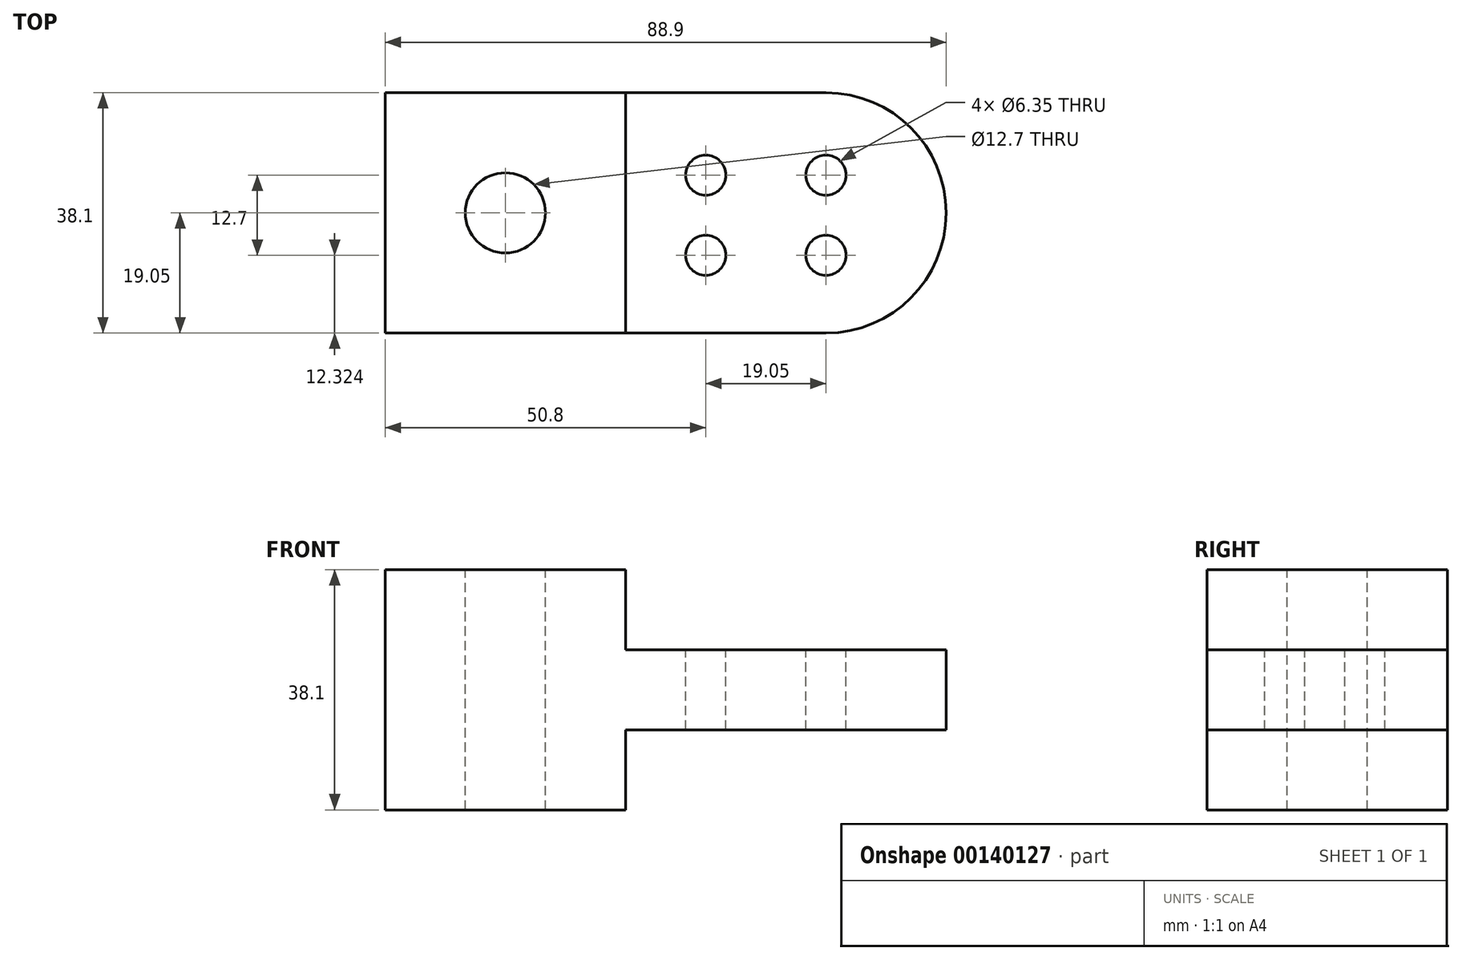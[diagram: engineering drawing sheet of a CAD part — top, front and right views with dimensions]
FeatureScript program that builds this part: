
annotation { "Feature Type Name" : "Feature", "Feature Type Description" : "" }
export const myFeature = defineFeature(function(context is Context, id is Id, definition is map)
    precondition{}
    {
        {
            var Q0;
            Q0=qCreatedBy(makeId("Top.planeOp"),FACE);
            var sketch = newSketch(context, id + "F0", { "sketchPlane" : qUnion([Q0])});
            skLineSegment(sketch, "E0.bottom", {"start": v(0, 0) * mm, "end": v(38.1, 0) * mm});
            skLineSegment(sketch, "E0.top", {"start": v(0, 38.1) * mm, "end": v(38.1, 38.1) * mm});
            skLineSegment(sketch, "E0.left", {"start": v(0, 0) * mm, "end": v(0, 38.1) * mm});
            skLineSegment(sketch, "E0.right", {"start": v(38.1, 0) * mm, "end": v(38.1, 38.1) * mm});
            skLineSegment(sketch, "E1.bottom", {"start": v(38.1, 38.1) * mm, "end": v(69.85, 38.1) * mm});
            skLineSegment(sketch, "E1.top", {"start": v(38.1, 0) * mm, "end": v(69.85, 0) * mm});
            skLineSegment(sketch, "E1.left", {"start": v(38.1, 38.1) * mm, "end": v(38.1, 0) * mm});
            skLineSegment(sketch, "E1.right", {"start": v(69.85, 38.1) * mm, "end": v(69.85, 0) * mm});
            skArc(sketch, "E2", {"start": v(69.85, 0) * mm, "mid": v(88.9, 19.05) * mm, "end": v(69.85, 38.1) * mm});
            skSolve(sketch);
        }
        {
            var Q0;
            Q0=makeQuery(id+"F0.imprint","IMPRINT",FACE,{"disambiguationData":[TD([[makeQuery(id+"F0.imprint","IMPRINT",EDGE,{"derivedFrom":sQuery(id+"F0.wireOp",EDGE,"E0.bottom")}),1.0]])]});
            extrude(context, id + "F1", {"entities" : qUnion([Q0]), "endBound" : BoundingType.SYMMETRIC, "depth" : 38.1 * mm});
        }
        {
            var Q0;
            Q0=makeQuery(id+"F0.imprint","IMPRINT",FACE,{"disambiguationData":[TD([[makeQuery(id+"F0.imprint","IMPRINT",EDGE,{"derivedFrom":sQuery(id+"F0.wireOp",EDGE,"E1.bottom")}),-1.0]])]});
            var Q1;
            Q1=makeQuery(id+"F0.imprint","IMPRINT",FACE,{"disambiguationData":[TD([[makeQuery(id+"F0.imprint","IMPRINT",EDGE,{"derivedFrom":sQuery(id+"F0.wireOp",EDGE,"E1.right")}),1.0]])]});
            extrude(context, id + "F2", {"entities" : qUnion([Q0, Q1]), "operationType" : NewBodyOperationType.ADD, "endBound" : BoundingType.SYMMETRIC, "depth" : 12.7 * mm});
        }
        {
            var Q0;
            Q0=makeQuery(id+"F1.opExtrude","CAP_FACE",FACE,{"disambiguationData":[OSD([sQuery(id+"F0.wireOp",EDGE,"E0.bottom"),sQuery(id+"F0.wireOp",EDGE,"E0.top"),sQuery(id+"F0.wireOp",EDGE,"E0.left"),sQuery(id+"F0.wireOp",EDGE,"E1.left")])],"isStart":false});
            var sketch = newSketch(context, id + "F3", { "sketchPlane" : qUnion([Q0])});
            skPoint(sketch, "E3", {"position": v(19.05, 19.05) * mm});
            skPoint(sketch, "E3.positionSnap0", {"position": v(19.05, 0) * mm});
            skSolve(sketch);
        }
        {
            var Q0;
            Q0=sQuery(id+"F3.wireOp",VERTEX,"E3");
            var Q1;
            Q1=makeQuery(id+"F1.opExtrude","SWEPT_BODY",BODY,{"disambiguationData":[OSD([sQuery(id+"F0.wireOp",EDGE,"E0.bottom"),sQuery(id+"F0.wireOp",EDGE,"E0.top"),sQuery(id+"F0.wireOp",EDGE,"E0.left"),sQuery(id+"F0.wireOp",EDGE,"E1.left")])]});
            hole(context, id + "F4", {"style" : HoleStyle.SIMPLE, "endStyle" : HoleEndStyle.THROUGH, "holeDiameter" : 12.7 * mm, "locations" : qUnion([Q0]), "scope" : qUnion([Q1]), "isTappedThrough" : true});
        }
        {
            var Q0;
            Q0=makeQuery(id+"F2.opExtrude","CAP_FACE",FACE,{"disambiguationData":[OSD([sQuery(id+"F0.wireOp",EDGE,"E1.bottom"),sQuery(id+"F0.wireOp",EDGE,"E1.top"),sQuery(id+"F0.wireOp",EDGE,"E1.left"),sQuery(id+"F0.wireOp",EDGE,"E2")])],"isStart":false});
            var sketch = newSketch(context, id + "F5", { "sketchPlane" : qUnion([Q0])});
            skPoint(sketch, "E4", {"position": v(50.8, 12.32) * mm});
            skPoint(sketch, "E5", {"position": v(69.85, 12.32) * mm});
            skPoint(sketch, "E6", {"position": v(69.85, 25.02) * mm});
            skPoint(sketch, "E7", {"position": v(50.8, 25.02) * mm});
            skSolve(sketch);
        }
        {
            var Q0;
            Q0=sQuery(id+"F5.wireOp",VERTEX,"E7");
            var Q1;
            Q1=sQuery(id+"F5.wireOp",VERTEX,"E4");
            var Q2;
            Q2=sQuery(id+"F5.wireOp",VERTEX,"E5");
            var Q3;
            Q3=sQuery(id+"F5.wireOp",VERTEX,"E6");
            var Q4;
            Q4=makeQuery(id+"F1.opExtrude","SWEPT_BODY",BODY,{"disambiguationData":[OSD([sQuery(id+"F0.wireOp",EDGE,"E0.bottom"),sQuery(id+"F0.wireOp",EDGE,"E0.top"),sQuery(id+"F0.wireOp",EDGE,"E0.left"),sQuery(id+"F0.wireOp",EDGE,"E1.left")])]});
            hole(context, id + "F6", {"style" : HoleStyle.SIMPLE, "endStyle" : HoleEndStyle.THROUGH, "holeDiameter" : 6.35 * mm, "locations" : qUnion([Q0, Q1, Q2, Q3]), "scope" : qUnion([Q4]), "isTappedThrough" : true});
        }
    });
